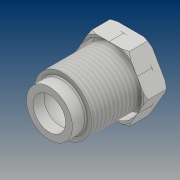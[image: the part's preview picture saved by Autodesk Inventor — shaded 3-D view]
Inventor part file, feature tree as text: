
AUTODESK INVENTOR PART (.ipt)
format: ipt  version: 2021 (Build 250183000, 183)  size: 241,152 bytes
history: native  units: mm
features: sketch x4, revolve x2, thread x2, fillet x2, projected_geometry x2, extrude x1, plane x1, mirror x1
ambient origin geometry x8: Origin, YZ Plane, XZ Plane, XY Plane, X Axis, Y Axis, Z Axis, Center Point
bodies: Solid1 (feature_tree)
feature tree (15):
  revolve  "Revolution1"  [1 undecoded]
  extrude  "Extrusion1"  Depth=5.0mm
  revolve  "Revolution2"  [1 undecoded]
  sketch  "Sketch5"  dims[d20=17.0mm d21=0.8mm d22=2.5mm d23=0.5mm d24=90.0deg d25=8.0mm d26=0.0mm d27=90.0deg d36=0.5mm d38=0.5mm d39=1.5mm d40=-4.0mm d41=9.0mm d42=0.0mm d43=22.5mm d44=0.0mm d45=0.5mm d46=0.5mm]
  plane  "Work Plane2"
  mirror  "Mirror2"
  thread  "Thread1"  [1 undecoded]
  thread  "Thread2"  [1 undecoded]
  fillet  "Fillet1"  Radius=24.0mm
  fillet  "Fillet2"  Radius=16.0mm
  sketch  "Sketch1"  dims[d6=14.0mm d7=17.0mm]
  sketch  "Sketch2"  dims[d8=21.0mm d10=5.0mm]
  sketch  "Sketch3"  dims[d11=12.0mm d12=4.0mm d13=30.0mm d14=5.0mm d18=24.0mm d19=16.0mm]
  projected_geometry  "Projected Loop1"
  projected_geometry  "Projected Loop2"
note: 4 required parameter values undecoded (feature->parameter linkage not recoverable at this tier; creation-order binding heuristic only, values carry confidence <= 0.55)